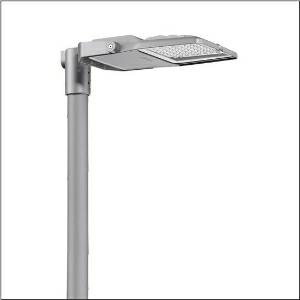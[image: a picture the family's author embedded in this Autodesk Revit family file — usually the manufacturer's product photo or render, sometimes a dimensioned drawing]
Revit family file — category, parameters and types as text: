
# Revit family: floodlight_fl_21_iq_mini___pl33t_5xa7772d2f3a_d038
name_source: partatom
category: Lighting Fixtures
units: mm (PartAtom-declared; Revit-internal decimal feet)

## family parameters
Cut with Voids When Loaded = No
Host = Face
Light Source = No
Part Type = Normal
Room Calculation Point = No
Round Connector Dimension = Use Diameter
Shared = No

## types (1)
- --- (1 x LED, 17620 lm, 143 W, 3000K)
    Apparent Load = 143 VA
    CIE Flux Codes = 26 75 99 100 100
    Color Rendering = 70
    Color Temperature = 3000K
    Default Elevation = 1800 mm
    Description = Floodlight FL 21 iQ mini, floodlight, primary light control with lens, of PMMA, primary optical cover: protective disc, of toughened safety glass, transparent, light distribution: PL33T, light emission: direct distribution, installation type: surface-mounted, LED, High Power LED, rated luminous flux: 17.620lm, luminous efficacy: 123lm/W, light colour: 730, colour temperature: 3000K, control gear: iQ Street-Remote/DALI, control: Auto-Match, Temp-Guard, Night-Set, Smart-Wire, Desk-Remote (wireless, voltage-free reading and setting of iQ features in the workshop via application-optimized NFC function/RFID function), optimised constant luminous flux control (CLO 2.0), Light-Fading, Lumen-Switch, with terminal, 6-pole, mains connection: 220..240V, AC, 50/60Hz, start of lifetime: 143W, end of service life: 152W, reduction: 61W, luminaire housing, of diecast aluminium, powder-coated, Siteco® metallic grey (DB 702S), corrosivity category C5 mid according to DIN EN ISO 12944, suitable for swimming pools, chlorine-resistant, sealing non-destructively replaceable, please order mast flange separately, mast bracket, of steel, galvanised, powder-coated, protection rating (complete): IP66, insulation class (complete): insulation class II (safety insulation), certification: CE, ENEC, VDE, protection symbol: D, impact resistance: IK08, permissible operating ambient temperature: -40..+40°C, permissible operating ambient temperature for outdoor applications: -40..+50°C, standard: DIN EN 12944, LABS conformity tested according to VDMA 24364:2018-05, packaging unit: 1 piece

Light Distribution: PL33T
    Height = 70 mm
    Lamp = 1 x LED
    Lamp Light Flux = 17620 lm
    Lamp Power = 143 W
    Lamp count = 1
    Length = 485 mm
    Luminous efficacy = 123 lm/W
    Manufacturer = Siteco
    ModVariant = No
    Model = 5XA7772D2F3A
    Number of Poles = 1
    OnlyDefault = Yes
    Power Factor = 1
    Product Name = Floodlight FL 21 iQ mini | PL33T
    Product group = floodlight | pylon annexe
    ProductGroupID = 6200
    Protection Class = Protection class II
    Protection Degree = IP 66
    RLX_Detail_Level = 1
    RLX_Emergency_Light_Flux = 0 lm
    RLX_Emergency_Type = 0
    RLX_Emergency_Type_DB = No
    RlxData = <blob elided: 101433 chars, md5=b02ce7f5>
    Socket = socket
    Standby Power = 0 W
    System Light Flux = 17620 lm
    System Power = 143 W
    Type Comments = factory setting: luminous flux: 100 % | dim-lin: 254 | 730 mA
    Type Image = l_1007125.jpg
    URL = http://relux.com
    VarID = @adj_148932
    Voltage = 0 V
    Weight = 0.00 kg
    Width = 337 mm

## geometry (parser evidence)
native form markers: Blend x4, Sweep x13
no freeform markers — native parametric forms only
